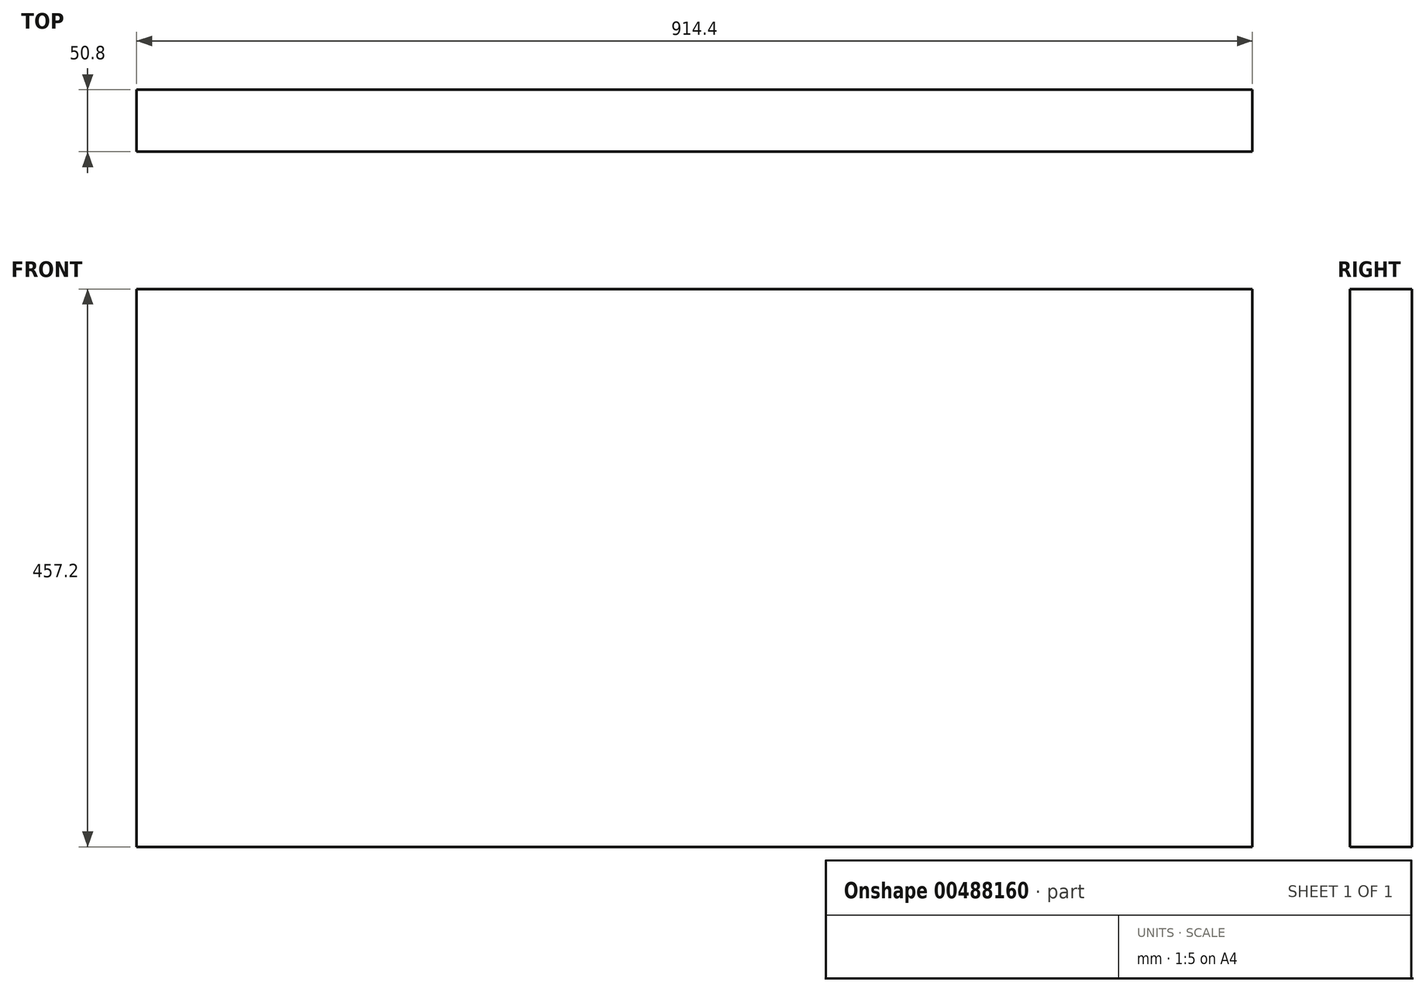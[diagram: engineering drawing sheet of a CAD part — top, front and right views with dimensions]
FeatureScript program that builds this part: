
annotation { "Feature Type Name" : "Feature", "Feature Type Description" : "" }
export const myFeature = defineFeature(function(context is Context, id is Id, definition is map)
    precondition{}
    {
        {
            var Q0;
            Q0=qCreatedBy(makeId("Front.planeOp"),FACE);
            var sketch = newSketch(context, id + "F0", { "sketchPlane" : qUnion([Q0])});
            skLineSegment(sketch, "E0", {"start": v(0, 0) * mm, "end": v(914.4, 0) * mm});
            skLineSegment(sketch, "E1", {"start": v(914.4, 0) * mm, "end": v(914.4, 457.2) * mm});
            skLineSegment(sketch, "E2", {"start": v(914.4, 457.2) * mm, "end": v(0, 457.2) * mm});
            skLineSegment(sketch, "E3", {"start": v(0, 457.2) * mm, "end": v(0, 0) * mm});
            skSolve(sketch);
        }
        {
            var Q0;
            Q0=makeQuery(id+"F0.imprint","IMPRINT",FACE,{"disambiguationData":[TD([[makeQuery(id+"F0.imprint","IMPRINT",EDGE,{"derivedFrom":sQuery(id+"F0.wireOp",EDGE,"E0")}),1.0]])]});
            extrude(context, id + "F1", {"entities" : qUnion([Q0]), "depth" : 50.8 * mm, "offsetDistance" : 25.4 * mm});
        }
    });
